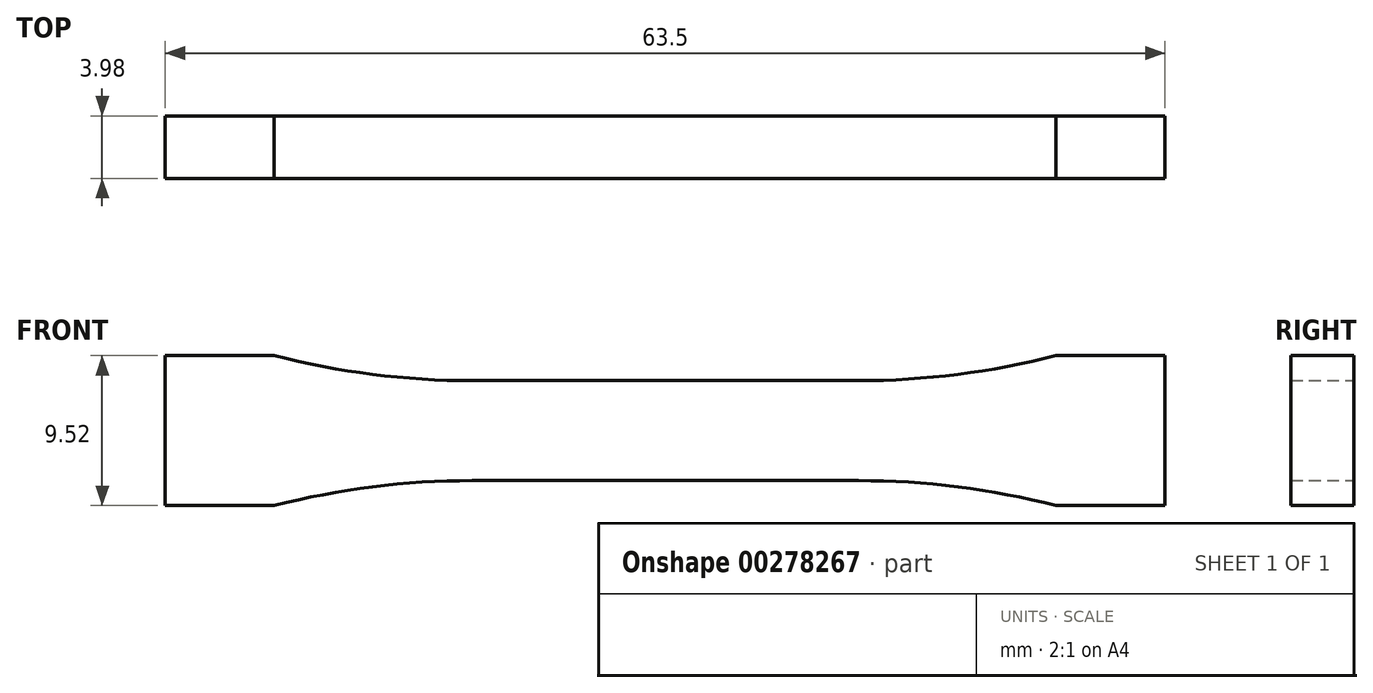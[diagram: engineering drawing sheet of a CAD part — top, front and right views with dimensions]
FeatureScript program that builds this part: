
annotation { "Feature Type Name" : "Feature", "Feature Type Description" : "" }
export const myFeature = defineFeature(function(context is Context, id is Id, definition is map)
    precondition{}
    {
        {
            var Q0;
            Q0=qCreatedBy(makeId("Front.planeOp"),FACE);
            var sketch = newSketch(context, id + "F0", { "sketchPlane" : qUnion([Q0])});
            skLineSegment(sketch, "E0", {"start": v(0, 3.18) * mm, "end": v(12.26, 3.18) * mm});
            skArc(sketch, "E1", {"start": v(12.26, 3.18) * mm, "mid": v(18.6, 3.57) * mm, "end": v(24.83, 4.76) * mm});
            skLineSegment(sketch, "E2", {"start": v(24.83, 4.76) * mm, "end": v(31.75, 4.76) * mm});
            skLineSegment(sketch, "E3.MirrorCS", {"start": v(24.83, -4.76) * mm, "end": v(31.75, -4.76) * mm});
            skLineSegment(sketch, "E4.MirrorCS", {"start": v(0, -3.17) * mm, "end": v(12.26, -3.17) * mm});
            skArc(sketch, "E5.MirrorCS", {"start": v(12.26, -3.18) * mm, "mid": v(18.6, -3.57) * mm, "end": v(24.83, -4.76) * mm});
            skLineSegment(sketch, "E6", {"start": v(31.75, 4.76) * mm, "end": v(31.75, -4.76) * mm});
            skLineSegment(sketch, "E7.MirrorCS", {"start": v(0, 3.18) * mm, "end": v(-12.26, 3.18) * mm});
            skArc(sketch, "E8.MirrorCS", {"start": v(-12.26, 3.18) * mm, "mid": v(-18.6, 3.57) * mm, "end": v(-24.83, 4.76) * mm});
            skLineSegment(sketch, "E9.MirrorCS", {"start": v(-24.83, 4.76) * mm, "end": v(-31.75, 4.76) * mm});
            skLineSegment(sketch, "E10.MirrorCS", {"start": v(-24.83, -4.76) * mm, "end": v(-31.75, -4.76) * mm});
            skLineSegment(sketch, "E11.MirrorCS", {"start": v(-31.75, 4.76) * mm, "end": v(-31.75, -4.76) * mm});
            skLineSegment(sketch, "E12.MirrorCS", {"start": v(0, -3.17) * mm, "end": v(-12.26, -3.17) * mm});
            skArc(sketch, "E13.MirrorCS", {"start": v(-12.26, -3.18) * mm, "mid": v(-18.6, -3.57) * mm, "end": v(-24.83, -4.76) * mm});
            skSolve(sketch);
        }
        {
            var Q0;
            Q0 = qSketchRegion(id + "F0", true);
            extrude(context, id + "F1", {"entities" : qUnion([Q0]), "endBound" : BoundingType.SYMMETRIC, "depth" : 4 * mm});
        }
    });
